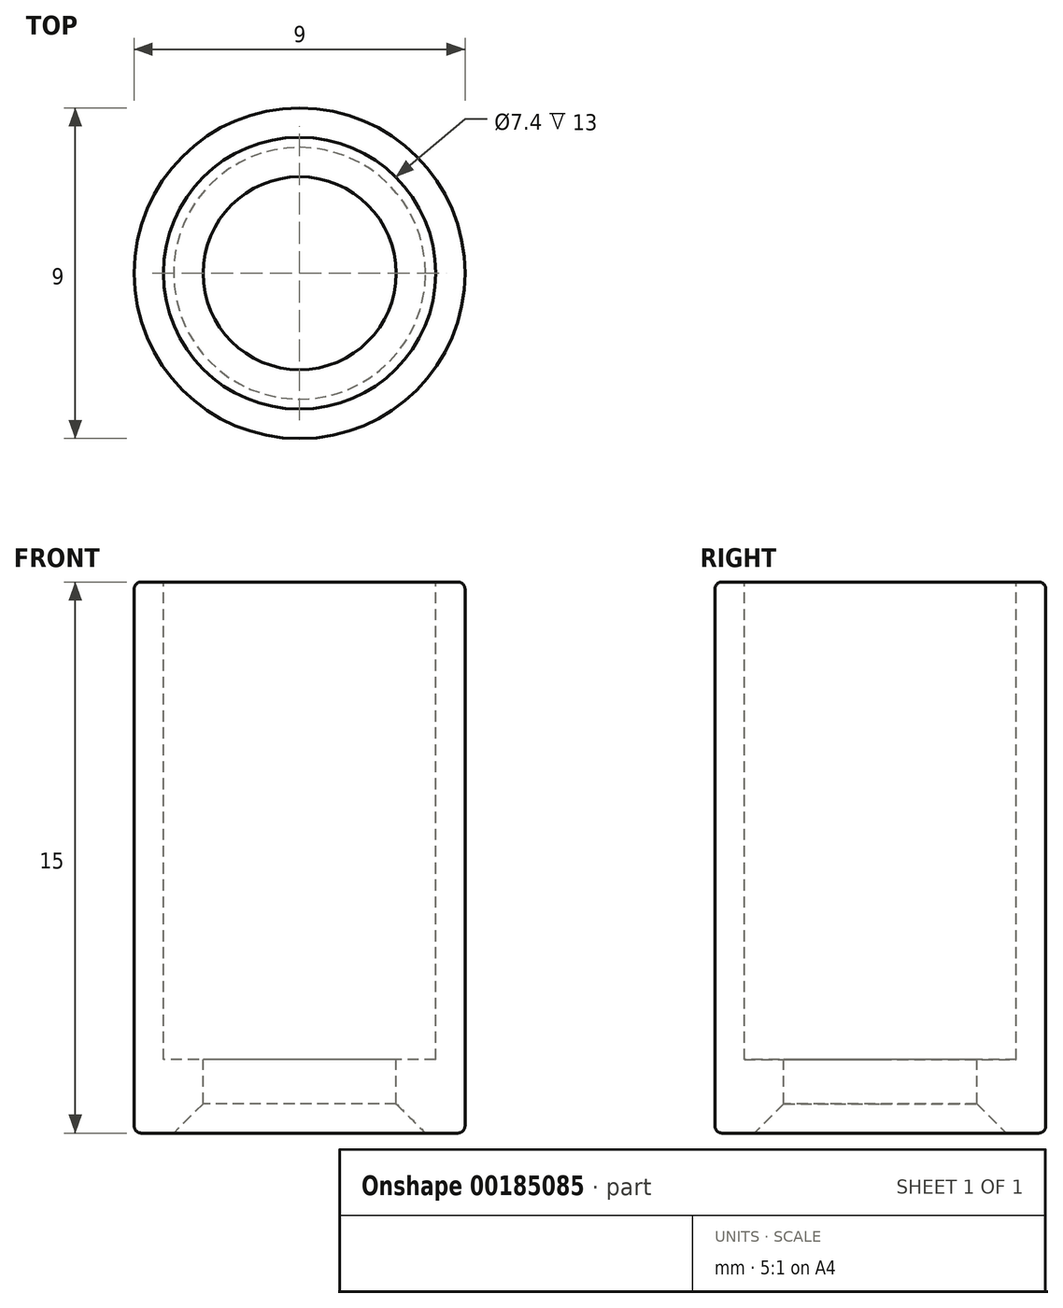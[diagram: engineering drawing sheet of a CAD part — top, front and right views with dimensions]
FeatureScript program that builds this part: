
annotation { "Feature Type Name" : "Feature", "Feature Type Description" : "" }
export const myFeature = defineFeature(function(context is Context, id is Id, definition is map)
    precondition{}
    {
        {
            var Q0;
            Q0=qCreatedBy(makeId("Top.planeOp"),FACE);
            var sketch = newSketch(context, id + "F0", { "sketchPlane" : qUnion([Q0])});
            skCircle(sketch, "E0", {"center": v(0, 0) * mm, "radius": 4.5 * mm});
            skSolve(sketch);
        }
        {
            var Q0;
            Q0 = qSketchRegion(id + "F0", true);
            extrude(context, id + "F1", {"entities" : qUnion([Q0]), "depth" : 15 * mm});
        }
        {
            var Q0;
            Q0=makeQuery(id+"F1.opExtrude","CAP_FACE",FACE,{"disambiguationData":[OSD([sQuery(id+"F0.wireOp",EDGE,"E0")])],"isStart":false});
            var sketch = newSketch(context, id + "F2", { "sketchPlane" : qUnion([Q0])});
            skCircle(sketch, "E1", {"center": v(0, 0) * mm, "radius": 2.62 * mm});
            skCircle(sketch, "E2", {"center": v(0, 0) * mm, "radius": 3.7 * mm});
            skSolve(sketch);
        }
        {
            var Q0;
            Q0=makeQuery(id+"F2.imprint","IMPRINT",FACE,{"disambiguationData":[TD([[makeQuery(id+"F2.imprint","IMPRINT",EDGE,{"derivedFrom":sQuery(id+"F2.wireOp",EDGE,"E1")}),1.0]])]});
            extrude(context, id + "F3", {"entities" : qUnion([Q0]), "operationType" : NewBodyOperationType.REMOVE, "oppositeDirection" : true, "depth" : 25 * mm});
        }
        {
            var Q0;
            Q0=makeQuery(id+"F2.imprint","IMPRINT",FACE,{"disambiguationData":[TD([[makeQuery(id+"F2.imprint","IMPRINT",EDGE,{"derivedFrom":sQuery(id+"F2.wireOp",EDGE,"E1")}),-1.0]])]});
            extrude(context, id + "F4", {"entities" : qUnion([Q0]), "operationType" : NewBodyOperationType.REMOVE, "oppositeDirection" : true, "depth" : 13 * mm});
        }
        {
            var Q0;
            Q0=makeQuery(id+"F1.opExtrude","CAP_EDGE",EDGE,{"disambiguationData":[OSD([sQuery(id+"F0.wireOp",EDGE,"E0")])],"isStart":false});
            var Q1;
            Q1=makeQuery(id+"F4.boolean.opBoolean","COPY",EDGE,{"derivedFrom":makeQuery(id+"F4.opExtrude","CAP_EDGE",EDGE,{"disambiguationData":[OSD([sQuery(id+"F2.wireOp",EDGE,"E2")])],"isStart":true})});
            var Q2;
            Q2=makeQuery(id+"F1.opExtrude","CAP_EDGE",EDGE,{"disambiguationData":[OSD([sQuery(id+"F0.wireOp",EDGE,"E0")])],"isStart":true});
            fillet(context, id + "F5", {"entities" : qUnion([Q0, Q1, Q2]), "radius" : 0.2 * mm, "tangentPropagation" : true, "allowEdgeOverflow" : false});
        }
        {
            var Q0;
            Q0=makeQuery(id+"F3.boolean.opBoolean","INTERSECT",EDGE,{"derivedFrom":[makeQuery(id+"F1.opExtrude","CAP_FACE",FACE,{"disambiguationData":[OSD([sQuery(id+"F0.wireOp",EDGE,"E0")])],"isStart":true}),makeQuery(id+"F3.opExtrude","SWEPT_FACE",FACE,{"disambiguationData":[OSD([sQuery(id+"F2.wireOp",EDGE,"E1")])]})]});
            chamfer(context, id + "F6", {"entities" : qUnion([Q0]), "width" : 0.8 * mm, "tangentPropagation" : true});
        }
    });
